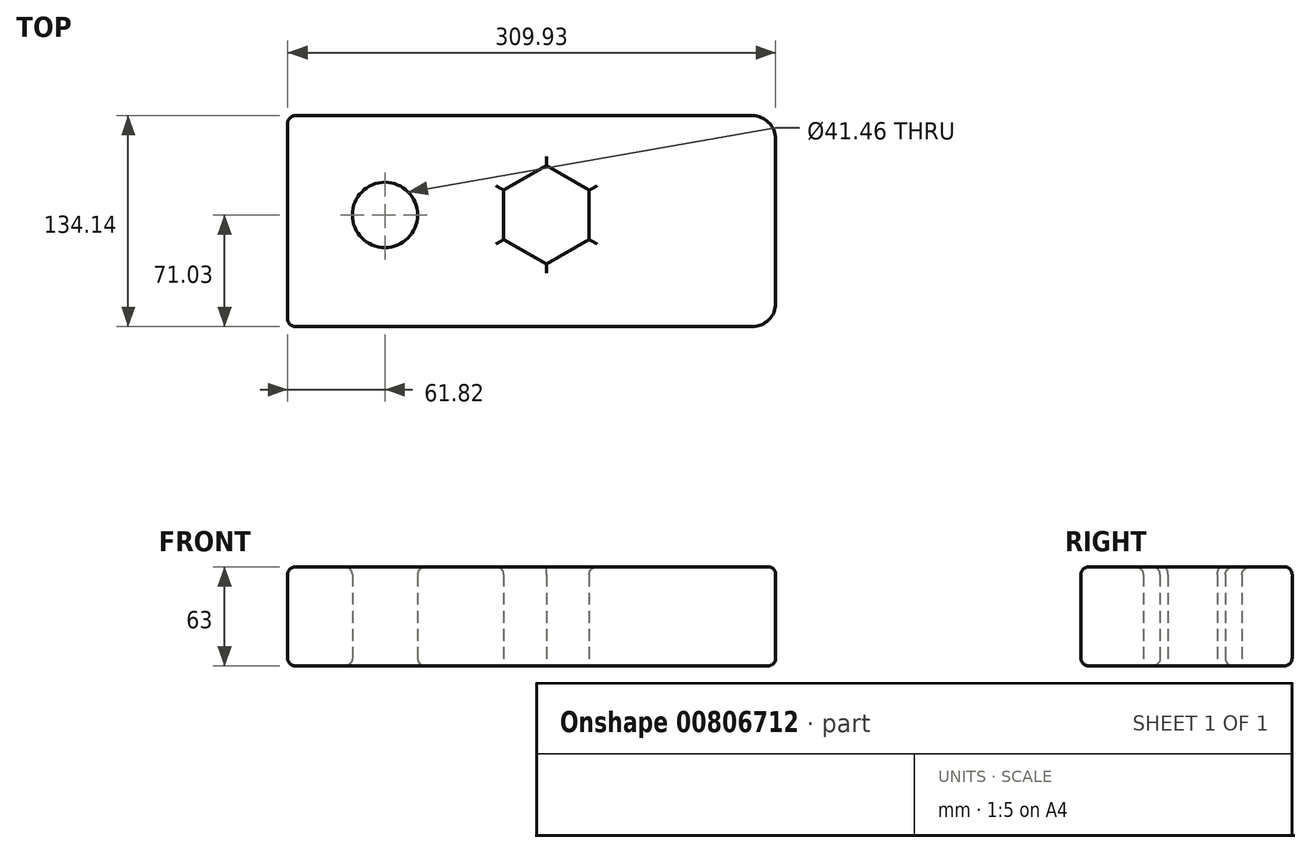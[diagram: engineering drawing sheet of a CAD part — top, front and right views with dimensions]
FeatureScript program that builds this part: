
annotation { "Feature Type Name" : "Feature", "Feature Type Description" : "" }
export const myFeature = defineFeature(function(context is Context, id is Id, definition is map)
    precondition{}
    {
        {
            var Q0;
            Q0=qCreatedBy(makeId("Top.planeOp"),FACE);
            var sketch = newSketch(context, id + "F0", { "sketchPlane" : qUnion([Q0])});
            skLineSegment(sketch, "E0.bottom", {"start": v(-144.08, 63.1) * mm, "end": v(150.85, 63.1) * mm});
            skLineSegment(sketch, "E0.top", {"start": v(-144.08, -71.03) * mm, "end": v(150.85, -71.03) * mm});
            skLineSegment(sketch, "E0.left", {"start": v(-144.08, 63.1) * mm, "end": v(-144.08, -71.03) * mm});
            skLineSegment(sketch, "E0.right", {"start": v(165.85, 48.1) * mm, "end": v(165.85, -56.03) * mm});
            skCircle(sketch, "E1", {"center": v(-82.26, 0) * mm, "radius": 20.73 * mm});
            skCircle(sketch, "E2.cCircle", {"center": v(20.28, 0) * mm, "radius": 27.1 * mm, "construction": true});
            skLineSegment(sketch, "E2.0", {"start": v(47.37, 15.64) * mm, "end": v(47.37, -15.64) * mm});
            skLineSegment(sketch, "E2.1", {"start": v(47.37, -15.64) * mm, "end": v(20.28, -31.28) * mm});
            skLineSegment(sketch, "E2.2", {"start": v(20.28, -31.28) * mm, "end": v(-6.81, -15.64) * mm});
            skLineSegment(sketch, "E2.3", {"start": v(-6.81, -15.64) * mm, "end": v(-6.81, 15.64) * mm});
            skLineSegment(sketch, "E2.4", {"start": v(-6.81, 15.64) * mm, "end": v(20.28, 31.28) * mm});
            skLineSegment(sketch, "E2.5", {"start": v(20.28, 31.28) * mm, "end": v(47.37, 15.64) * mm});
            skPoint(sketch, "E2.0.midPoint", {"position": v(47.37, 0) * mm});
            skPoint(sketch, "E3.visualSharp", {"position": v(165.85, 63.1) * mm});
            skArc(sketch, "E3.filletArc", {"start": v(165.85, 48.1) * mm, "mid": v(161.45, 58.71) * mm, "end": v(150.85, 63.1) * mm});
            skPoint(sketch, "E4.visualSharp", {"position": v(165.85, -71.03) * mm});
            skArc(sketch, "E4.filletArc", {"start": v(150.85, -71.03) * mm, "mid": v(161.45, -66.64) * mm, "end": v(165.85, -56.03) * mm});
            skSolve(sketch);
        }
        {
            var Q0;
            Q0=makeQuery(id+"F0.imprint","IMPRINT",FACE,{"disambiguationData":[TD([[makeQuery(id+"F0.imprint","IMPRINT",EDGE,{"derivedFrom":sQuery(id+"F0.wireOp",EDGE,"E0.bottom")}),-1.0]])]});
            extrude(context, id + "F1", {"entities" : qUnion([Q0]), "depth" : 63 * mm, "offsetDistance" : 25 * mm});
        }
        {
            var Q0;
            Q0=makeQuery(id+"F1.opExtrude","CAP_FACE",FACE,{"disambiguationData":[OSD([sQuery(id+"F0.wireOp",EDGE,"E0.bottom"),sQuery(id+"F0.wireOp",EDGE,"E0.top"),sQuery(id+"F0.wireOp",EDGE,"E0.left"),sQuery(id+"F0.wireOp",EDGE,"E0.right"),sQuery(id+"F0.wireOp",EDGE,"E1"),sQuery(id+"F0.wireOp",EDGE,"E2.0"),sQuery(id+"F0.wireOp",EDGE,"E2.1"),sQuery(id+"F0.wireOp",EDGE,"E2.2"),sQuery(id+"F0.wireOp",EDGE,"E2.3"),sQuery(id+"F0.wireOp",EDGE,"E2.4"),sQuery(id+"F0.wireOp",EDGE,"E2.5"),sQuery(id+"F0.wireOp",EDGE,"E3.filletArc"),sQuery(id+"F0.wireOp",EDGE,"E4.filletArc")])],"isStart":false});
            var Q1;
            Q1=makeQuery(id+"F1.opExtrude","SWEPT_EDGE",EDGE,{"disambiguationData":[OSD([sQuery(id+"F0.wireOp",EDGE,"E0.top"),sQuery(id+"F0.wireOp",EDGE,"E0.left")])]});
            var Q2;
            Q2=makeQuery(id+"F1.opExtrude","SWEPT_EDGE",EDGE,{"disambiguationData":[OSD([sQuery(id+"F0.wireOp",EDGE,"E0.bottom"),sQuery(id+"F0.wireOp",EDGE,"E0.left")])]});
            var Q3;
            Q3=makeQuery(id+"F1.opExtrude","CAP_EDGE",EDGE,{"disambiguationData":[OSD([sQuery(id+"F0.wireOp",EDGE,"E0.top")])],"isStart":true});
            var Q4;
            Q4=makeQuery(id+"F1.opExtrude","CAP_EDGE",EDGE,{"disambiguationData":[OSD([sQuery(id+"F0.wireOp",EDGE,"E0.left")])],"isStart":true});
            var Q5;
            Q5=makeQuery(id+"F1.opExtrude","SWEPT_FACE",FACE,{"disambiguationData":[OSD([sQuery(id+"F0.wireOp",EDGE,"E1")])]});
            fillet(context, id + "F2", {"entities" : qUnion([Q0, Q1, Q2, Q3, Q4, Q5]), "radius" : 5 * mm, "tangentPropagation" : true, "allowEdgeOverflow" : false});
        }
    });
